# Revit family: SM82T-B
name_source: partatom
category: Communication Devices
revit_build: Autodesk Revit 2014 (Build: 20140709_2115(x64)
units: mm (PartAtom-declared; Revit-internal decimal feet)

## types (1)
- Surface Mount Loundspeaker
    100V Taps = 0.94, 1.9, 3.8, 7.5, 15, 30, & 60 Watts / 8Ω Bypass
    70V Taps = 0.94, 1.9, 3.8, 7.5, 15, 30, & 60 Watts / 8Ω Bypass
    Baffle Material = <By Category>
    Body Material = QF_Plastic - Black - Fine Textured
    Color = <By Category>
    Cost = 343.99 $
    Cost MSRP = 343.99 $
    Coverage Horizontal = 110.00°
    Coverage Vertical = 110.00°
    Depth = 18.37 "
    Description = 8" 2-WAY ALL WEATHER LOUDSPEAKER WITH 60-WATT 70V/100V TRANSFORMER - BLACK
    Dispersion Angle = 0.00°
    Enclosure Material = <By Category>
    Environmental Testing = 100HR Salt Spray Test Per ASTM B117
    Family Code (default) = LOUD SPEAKERS
    Frequency Response  = 65Hz – 20kHz (±3dB)
    Grill Material = QF_Plastic - Black - Fine Textured
    Height = 9.81 "
    IQ Category = SPEAKERS
    Impedance = 8
    Ingress Protection = IP-33
    Input Connectors = Barrier Terminal
    Manufacturer = ATLAS SOUND
    Manufacturer URL = https://www.atlasied.com
    Market = Commercial, Higher Education, Emergency
    MasterFormat = 27 41 13
    MaterFormat Title = SPEAKERS
    Model = SM82T-B
    Mount Material = QF_Plastic - Black - Fine Textured
    OmniClass Number = 23-37 17 13 19
    OmniClass Title = SPEAKERS
    Pitch = 0.00°
    Power Rating (RMS) = 150 Watts
    Product Documentation Link = https://www.atlasied.com
    Product Page URL = https://www.atlasied.com
    Rotation = 0.00°
    SPL Max = 107
    ScheduleType |RF| = AtlasIED Master
    Sensitivity = 92
    Speaker Dispersion = 120.00°
    Transformer Option = Yes
    URL = www.atlassound.com
    Vertical Symmetry = Yes
    Warranty = 5 Year
    Weight Product = 17.25
    Width = 9.1 "

## geometry (parser evidence)
native form markers: Blend x2, Sweep x3
no freeform markers — native parametric forms only
